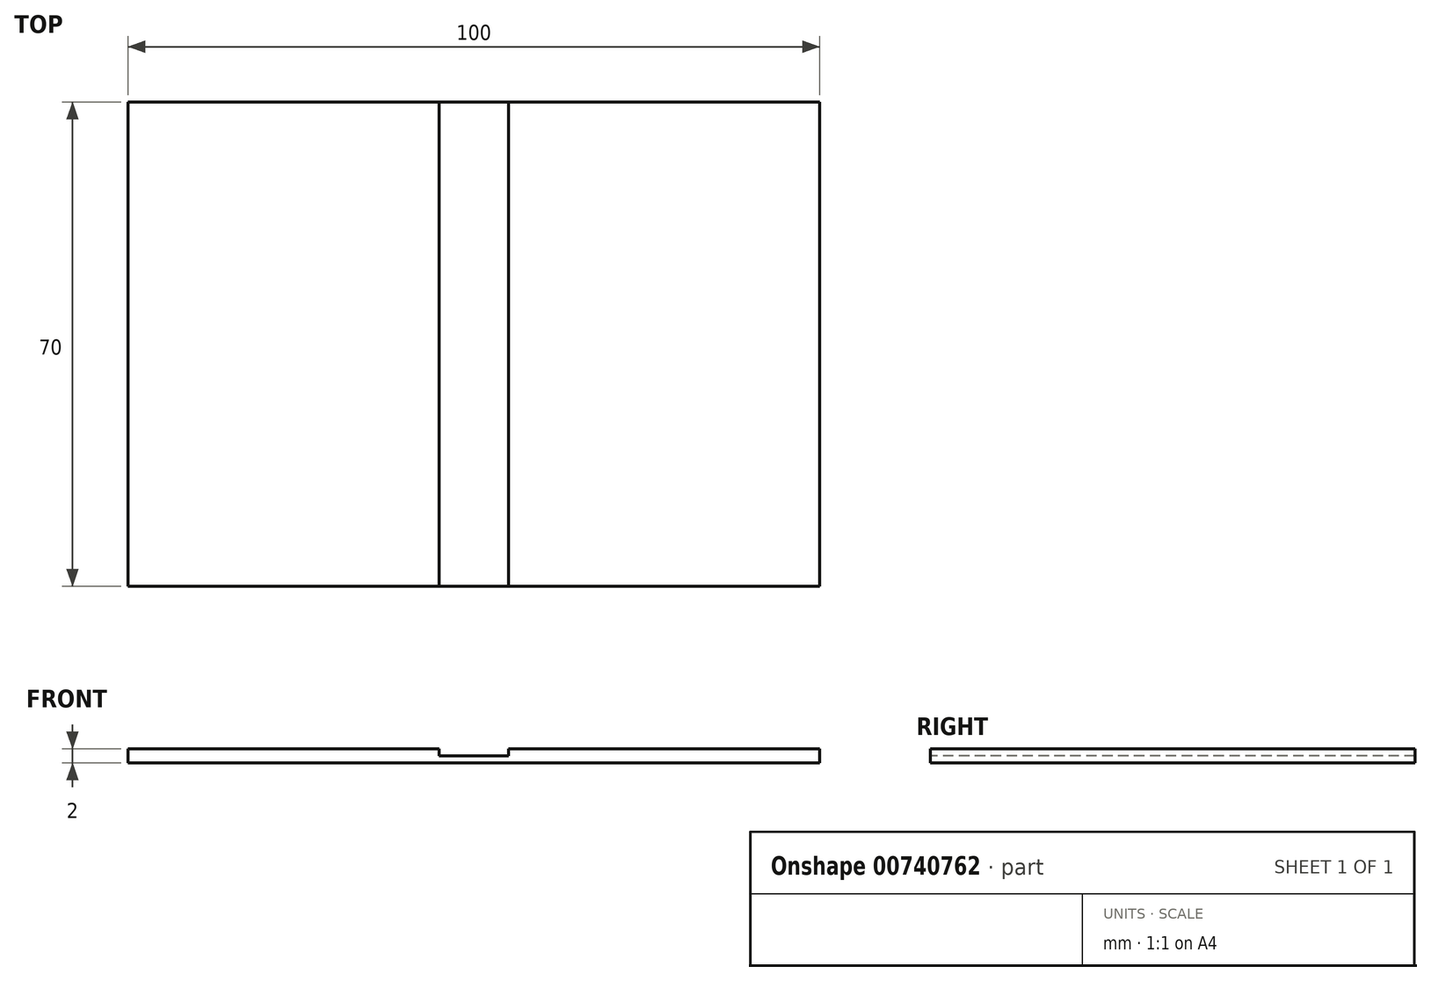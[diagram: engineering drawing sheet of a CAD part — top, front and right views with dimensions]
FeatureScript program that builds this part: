
annotation { "Feature Type Name" : "Feature", "Feature Type Description" : "" }
export const myFeature = defineFeature(function(context is Context, id is Id, definition is map)
    precondition{}
    {
        {
            var Q0;
            Q0=qCreatedBy(makeId("Top.planeOp"),FACE);
            var sketch = newSketch(context, id + "F0", { "sketchPlane" : qUnion([Q0])});
            skLineSegment(sketch, "E0.bottom", {"start": v(-110, 45) * mm, "end": v(110, 45) * mm});
            skLineSegment(sketch, "E0.top", {"start": v(-110, -45) * mm, "end": v(110, -45) * mm});
            skLineSegment(sketch, "E0.left", {"start": v(-110, 45) * mm, "end": v(-110, -45) * mm});
            skLineSegment(sketch, "E0.right", {"start": v(110, 45) * mm, "end": v(110, -45) * mm});
            skPoint(sketch, "E0.middle", {"position": v(0, 0) * mm});
            skSolve(sketch);
        }
        {
            var Q0;
            Q0=qCreatedBy(makeId("Top.planeOp"),FACE);
            var sketch = newSketch(context, id + "F1", { "sketchPlane" : qUnion([Q0])});
            skLineSegment(sketch, "E1.bottom", {"start": v(-50, 35) * mm, "end": v(50, 35) * mm});
            skLineSegment(sketch, "E1.top", {"start": v(-50, -35) * mm, "end": v(50, -35) * mm});
            skLineSegment(sketch, "E1.left", {"start": v(-50, 35) * mm, "end": v(-50, -35) * mm});
            skLineSegment(sketch, "E1.right", {"start": v(50, 35) * mm, "end": v(50, -35) * mm});
            skPoint(sketch, "E1.middle", {"position": v(0, 0) * mm});
            skSolve(sketch);
        }
        {
            var Q0;
            Q0=makeQuery(id+"F1.imprint","IMPRINT",FACE,{"disambiguationData":[TD([[makeQuery(id+"F1.imprint","IMPRINT",EDGE,{"derivedFrom":sQuery(id+"F1.wireOp",EDGE,"E1.bottom")}),-1.0]])]});
            extrude(context, id + "F2", {"entities" : qUnion([Q0]), "depth" : 2 * mm, "offsetDistance" : 25 * mm});
        }
        {
            var Q0;
            Q0=makeQuery(id+"F2.opExtrude","CAP_FACE",FACE,{"disambiguationData":[OSD([sQuery(id+"F1.wireOp",EDGE,"E1.bottom"),sQuery(id+"F1.wireOp",EDGE,"E1.top"),sQuery(id+"F1.wireOp",EDGE,"E1.left"),sQuery(id+"F1.wireOp",EDGE,"E1.right")])],"isStart":false});
            var sketch = newSketch(context, id + "F3", { "sketchPlane" : qUnion([Q0])});
            skLineSegment(sketch, "E2.bottom", {"start": v(-5, 35) * mm, "end": v(5, 35) * mm});
            skLineSegment(sketch, "E2.top", {"start": v(-5, -35) * mm, "end": v(5, -35) * mm});
            skLineSegment(sketch, "E2.left", {"start": v(-5, 35) * mm, "end": v(-5, -35) * mm});
            skLineSegment(sketch, "E2.right", {"start": v(5, 35) * mm, "end": v(5, -35) * mm});
            skPoint(sketch, "E2.middle", {"position": v(0, 0) * mm});
            skSolve(sketch);
        }
        {
            var Q0;
            Q0 = qSketchRegion(id + "F3", true);
            extrude(context, id + "F4", {"entities" : qUnion([Q0]), "operationType" : NewBodyOperationType.REMOVE, "oppositeDirection" : true, "depth" : 1 * mm, "offsetDistance" : 25 * mm});
        }
    });
